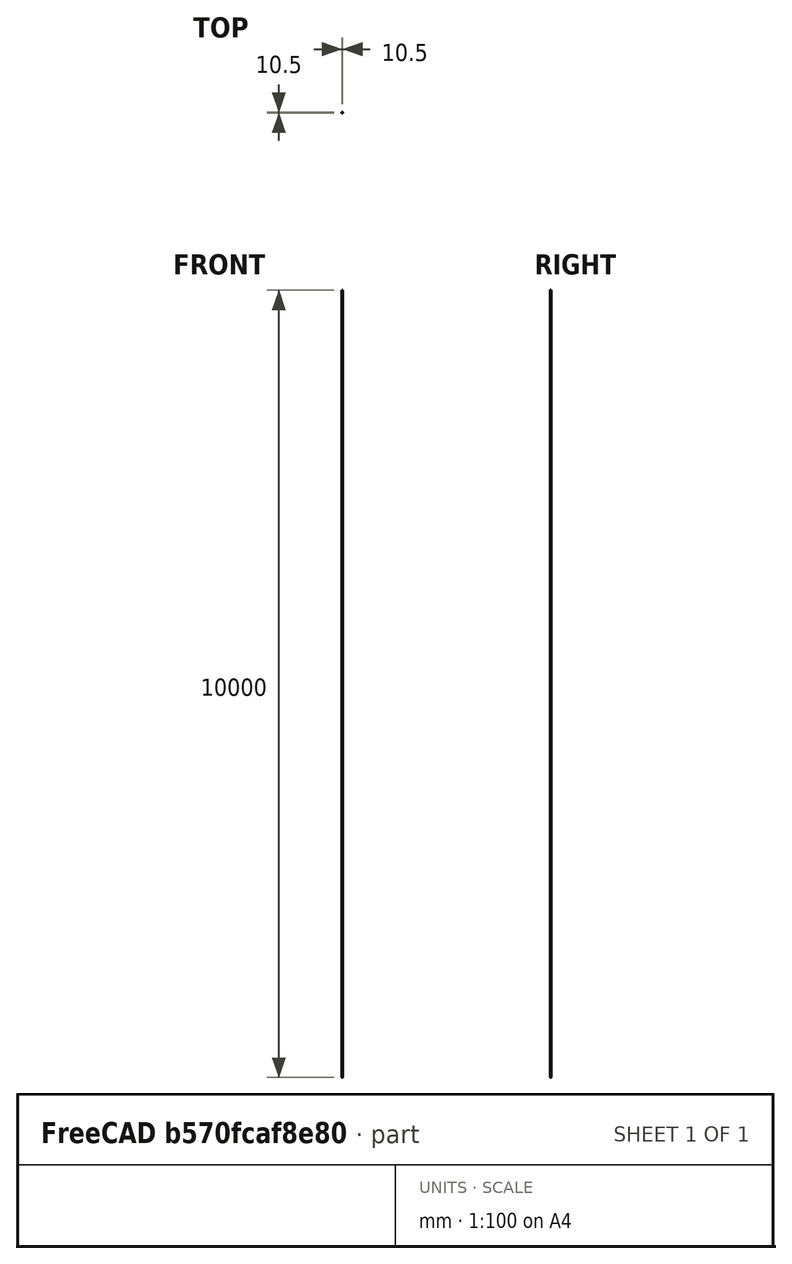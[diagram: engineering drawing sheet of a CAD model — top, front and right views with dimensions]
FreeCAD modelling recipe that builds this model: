
FCSTD DOCUMENT  (FreeCAD 0.16R)
Label: BarWedges
License: All rights reserved
LicenseURL: http://en.wikipedia.org/wiki/All_rights_reserved
objects: Sketcher::SketchObject×3, PartDesign::Pad×1, PartDesign::Revolution×1, Part::Cut×1, PartDesign::Pocket×1, Mesh::Feature×1
note: 10 computed .brp shape members not serialized (recipe doc carries the construction recipe); baked Part::Feature solids carry a one-line shape summary decoded from their .brp

FEATURE [Sketcher::SketchObject] Sketch
  Placement = pos=(0,0,0) rot=(1,0,0;1.5708rad)
  sketch-geometry (3):
    g0: LineSegment StartX=0 StartY=0 StartZ=0 EndX=-10 EndY=-17.3205 EndZ=0
    g1: LineSegment StartX=-10 StartY=-17.3205 StartZ=0 EndX=10 EndY=-17.3205 EndZ=0
    g2: LineSegment StartX=10 StartY=-17.3205 StartZ=0 EndX=0 EndY=0 EndZ=0
  constraints (8):
    c: Coincident(g0,g1)
    c: Coincident(g1,g2)
    c: Coincident(g2,g0)
    c: Equal(g0,g1)
    c: Equal(g0,g2)
    c: Symmetric(g1,g0,g-2)
    c: Coincident(g0,g-1)
    c: Distance(g2) = 20
FEATURE [PartDesign::Pad] Pad
  Length = 50
  Length2 = 100
  Midplane = true
  Placement = pos=(0,0,0) rot=(1,0,0;1.5708rad)
  Sketch = -> Sketch
  Type = 0
FEATURE [Sketcher::SketchObject] Sketch001
  Placement = pos=(0,0,0) rot=(1,0,0;1.5708rad)
  sketch-geometry (4):
    g0: LineSegment StartX=5.25 StartY=50 StartZ=0 EndX=40.25 EndY=50 EndZ=0
    g1: LineSegment StartX=40.25 StartY=50 StartZ=0 EndX=40.25 EndY=-50 EndZ=0
    g2: LineSegment StartX=40.25 StartY=-50 StartZ=0 EndX=5.25 EndY=-50 EndZ=0
    g3: LineSegment StartX=5.25 StartY=-50 StartZ=0 EndX=5.25 EndY=50 EndZ=0
  constraints (12):
    c: Coincident(g0,g1)
    c: Coincident(g1,g2)
    c: Coincident(g2,g3)
    c: Coincident(g3,g0)
    c: Horizontal(g0)
    c: Horizontal(g2)
    c: Vertical(g1)
    c: Vertical(g3)
    c: DistanceX(g-2,g0) = 5.25
    c: Symmetric(g0,g2,g-1)
    c: Distance(g3) = 100
    c: Distance(g0) = 35
FEATURE [PartDesign::Revolution] Revolution
  Angle = 360
  Axis = (0,0,1)
  Base = (0,0,0)
  Placement = pos=(0,0,0) rot=(1,0,0;1.5708rad)
  ReferenceAxis = -> Sketch001 [V_Axis]
  Reversed = true
  Sketch = -> Sketch001
FEATURE [Part::Cut] Cut
  Base = -> Pad
  Tool = -> Revolution
FEATURE [Sketcher::SketchObject] Sketch002
  Placement = pos=(0,0,-17.3205) rot=(1,0,0;3.14159rad)
  Support = -> Cut [Face4]
  sketch-geometry (1):
    g0: Circle CenterX=0 CenterY=0 CenterZ=0 NormalX=0 NormalY=0 NormalZ=1 Radius=2.7
  constraints (2):
    c: Radius(g0) = 2.7
    c: Coincident(g-1,g0)
FEATURE [PartDesign::Pocket] Pocket
  Length = 5
  Sketch = -> Sketch002
  Type = 1
FEATURE [Mesh::Feature] Mesh  label="Pocket (Meshed)"
